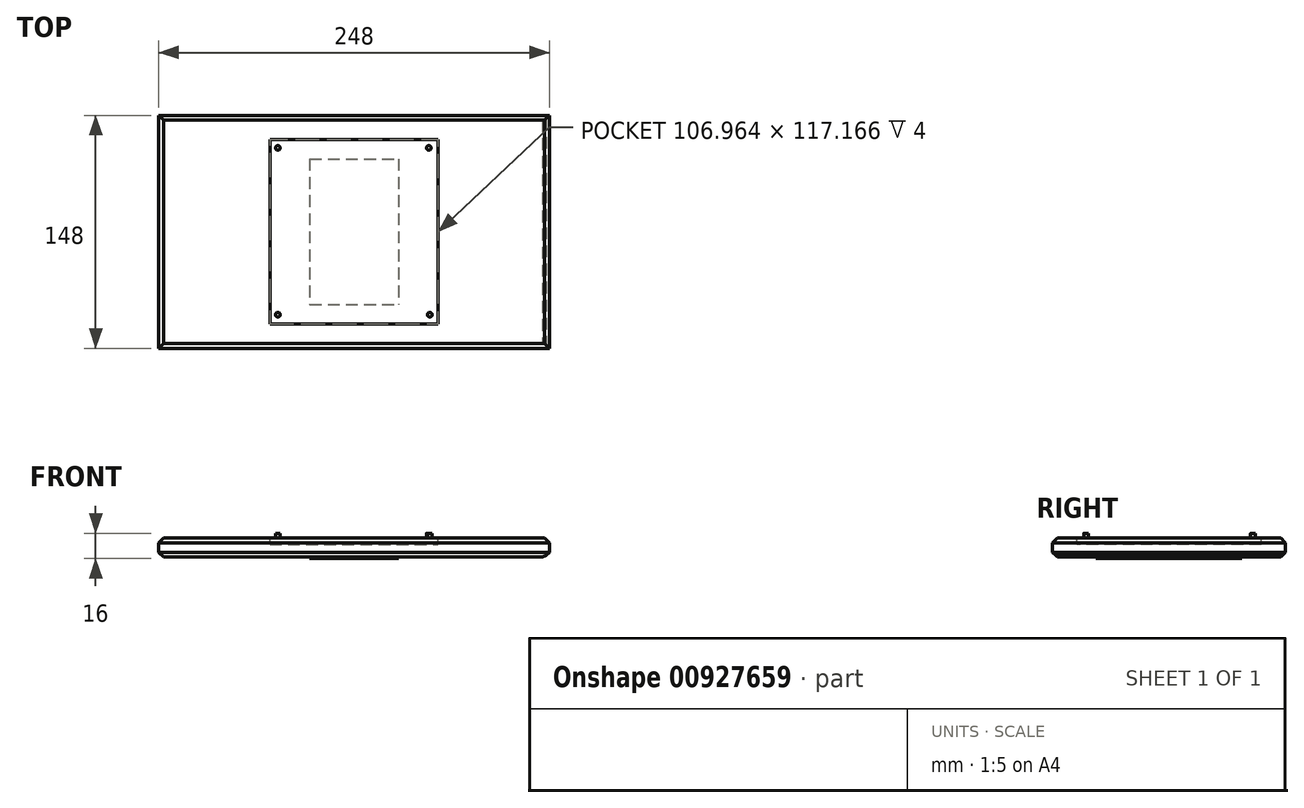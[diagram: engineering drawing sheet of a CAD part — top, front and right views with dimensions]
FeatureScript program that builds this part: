
annotation { "Feature Type Name" : "Feature", "Feature Type Description" : "" }
export const myFeature = defineFeature(function(context is Context, id is Id, definition is map)
    precondition{}
    {
        {
            var Q0;
            Q0=qCreatedBy(makeId("Top.planeOp"),FACE);
            var sketch = newSketch(context, id + "F0", { "sketchPlane" : qUnion([Q0])});
            skLineSegment(sketch, "E0.bottom", {"start": v(-124, -74) * mm, "end": v(124, -74) * mm});
            skLineSegment(sketch, "E0.top", {"start": v(-124, 74) * mm, "end": v(124, 74) * mm});
            skLineSegment(sketch, "E0.left", {"start": v(-124, -74) * mm, "end": v(-124, 74) * mm});
            skLineSegment(sketch, "E0.right", {"start": v(124, -74) * mm, "end": v(124, 74) * mm});
            skPoint(sketch, "E0.middle", {"position": v(0, 0) * mm});
            skSolve(sketch);
        }
        {
            var Q0;
            Q0 = qSketchRegion(id + "F0", true);
            extrude(context, id + "F1", {"entities" : qUnion([Q0]), "depth" : 12 * mm, "offsetDistance" : 25 * mm});
        }
        {
            var Q0;
            Q0=makeQuery(id+"F1.opExtrude","CAP_EDGE",EDGE,{"disambiguationData":[OSD([sQuery(id+"F0.wireOp",EDGE,"E0.top")])],"isStart":false});
            var Q1;
            Q1=makeQuery(id+"F1.opExtrude","CAP_EDGE",EDGE,{"disambiguationData":[OSD([sQuery(id+"F0.wireOp",EDGE,"E0.left")])],"isStart":false});
            var Q2;
            Q2=makeQuery(id+"F1.opExtrude","CAP_EDGE",EDGE,{"disambiguationData":[OSD([sQuery(id+"F0.wireOp",EDGE,"E0.bottom")])],"isStart":false});
            var Q3;
            Q3=makeQuery(id+"F1.opExtrude","CAP_EDGE",EDGE,{"disambiguationData":[OSD([sQuery(id+"F0.wireOp",EDGE,"E0.right")])],"isStart":true});
            chamfer(context, id + "F2", {"entities" : qUnion([Q0, Q1, Q2, Q3]), "width" : 3 * mm, "tangentPropagation" : true});
        }
        {
            var Q0;
            Q0=makeQuery(id+"F1.opExtrude","CAP_EDGE",EDGE,{"disambiguationData":[OSD([sQuery(id+"F0.wireOp",EDGE,"E0.left")])],"isStart":true});
            var Q1;
            Q1=makeQuery(id+"F1.opExtrude","CAP_EDGE",EDGE,{"disambiguationData":[OSD([sQuery(id+"F0.wireOp",EDGE,"E0.top")])],"isStart":true});
            var Q2;
            Q2=makeQuery(id+"F1.opExtrude","CAP_EDGE",EDGE,{"disambiguationData":[OSD([sQuery(id+"F0.wireOp",EDGE,"E0.bottom")])],"isStart":true});
            var Q3;
            {var subQ0=sQuery(id+"F0.wireOp",EDGE,"E0.right");Q3=makeQuery(id+"F2.opChamfer","BLEND_EDGE",EDGE,{"blendedFrom":[makeQuery(id+"F1.opExtrude","CAP_EDGE",EDGE,{"disambiguationData":[OSD([subQ0])],"isStart":true}),makeQuery(id+"F1.opExtrude","CAP_FACE",FACE,{"disambiguationData":[OSD([sQuery(id+"F0.wireOp",EDGE,"E0.bottom"),sQuery(id+"F0.wireOp",EDGE,"E0.top"),sQuery(id+"F0.wireOp",EDGE,"E0.left"),subQ0])],"isStart":true})],"blendedInto":[makeQuery(id+"F1.opExtrude","CAP_FACE",FACE,{"disambiguationData":[OSD([sQuery(id+"F0.wireOp",EDGE,"E0.bottom"),sQuery(id+"F0.wireOp",EDGE,"E0.top"),sQuery(id+"F0.wireOp",EDGE,"E0.left"),subQ0])],"isStart":true})]});}
            chamfer(context, id + "F3", {"entities" : qUnion([Q0, Q1, Q2, Q3]), "width" : 3 * mm, "tangentPropagation" : true});
        }
        {
            var Q0;
            Q0=qCreatedBy(makeId("Top.planeOp"),FACE);
            var sketch = newSketch(context, id + "F4", { "sketchPlane" : qUnion([Q0])});
            skLineSegment(sketch, "E1.bottom", {"start": v(-28.16, 46.29) * mm, "end": v(28.16, 46.29) * mm});
            skLineSegment(sketch, "E1.top", {"start": v(-28.16, -46.29) * mm, "end": v(28.16, -46.29) * mm});
            skLineSegment(sketch, "E1.left", {"start": v(-28.16, 46.29) * mm, "end": v(-28.16, -46.29) * mm});
            skLineSegment(sketch, "E1.right", {"start": v(28.16, 46.29) * mm, "end": v(28.16, -46.29) * mm});
            skPoint(sketch, "E1.middle", {"position": v(0, 0) * mm});
            skSolve(sketch);
        }
        {
            var Q0;
            Q0 = qSketchRegion(id + "F4", true);
            extrude(context, id + "F5", {"entities" : qUnion([Q0]), "oppositeDirection" : true, "depth" : 1 * mm, "offsetDistance" : 25 * mm});
        }
        {
            var Q0;
            Q0=makeQuery(id+"F1.opExtrude","CAP_FACE",FACE,{"disambiguationData":[OSD([sQuery(id+"F0.wireOp",EDGE,"E0.bottom"),sQuery(id+"F0.wireOp",EDGE,"E0.top"),sQuery(id+"F0.wireOp",EDGE,"E0.left"),sQuery(id+"F0.wireOp",EDGE,"E0.right")])],"isStart":false});
            var sketch = newSketch(context, id + "F6", { "sketchPlane" : qUnion([Q0])});
            skLineSegment(sketch, "E2.bottom", {"start": v(-53.48, 58.58) * mm, "end": v(53.48, 58.58) * mm});
            skLineSegment(sketch, "E2.top", {"start": v(-53.48, -58.58) * mm, "end": v(53.48, -58.58) * mm});
            skLineSegment(sketch, "E2.left", {"start": v(-53.48, 58.58) * mm, "end": v(-53.48, -58.58) * mm});
            skLineSegment(sketch, "E2.right", {"start": v(53.48, 58.58) * mm, "end": v(53.48, -58.58) * mm});
            skPoint(sketch, "E2.middle", {"position": v(0, 0) * mm});
            skSolve(sketch);
        }
        {
            var Q0;
            Q0 = qSketchRegion(id + "F6", true);
            extrude(context, id + "F7", {"entities" : qUnion([Q0]), "operationType" : NewBodyOperationType.REMOVE, "oppositeDirection" : true, "depth" : 4 * mm, "offsetDistance" : 25 * mm});
        }
        {
            var Q0;
            Q0=makeQuery(id+"F7.boolean.opBoolean","COPY",FACE,{"derivedFrom":makeQuery(id+"F7.opExtrude","CAP_FACE",FACE,{"disambiguationData":[OSD([sQuery(id+"F6.wireOp",EDGE,"E2.bottom"),sQuery(id+"F6.wireOp",EDGE,"E2.top"),sQuery(id+"F6.wireOp",EDGE,"E2.left"),sQuery(id+"F6.wireOp",EDGE,"E2.right")])],"isStart":false})});
            var sketch = newSketch(context, id + "F8", { "sketchPlane" : qUnion([Q0])});
            skSolve(sketch);
        }
        {
            var Q0;
            Q0=makeQuery(id+"F8.imprint","IMPRINT",FACE,{"disambiguationData":[TD([[makeQuery(id+"F8.imprint","IMPRINT",EDGE,{"derivedFrom":makeQuery(id+"F7.boolean.opBoolean","COPY",EDGE,{"derivedFrom":makeQuery(id+"F7.opExtrude","CAP_EDGE",EDGE,{"disambiguationData":[OSD([sQuery(id+"F6.wireOp",EDGE,"E2.bottom")])],"isStart":false})})}),-1.0]])]});
            extrude(context, id + "F9", {"entities" : qUnion([Q0]), "depth" : 4 * mm, "offsetDistance" : 25 * mm});
        }
        {
            var Q0;
            Q0=makeQuery(id+"F9.opExtrude","CAP_FACE",FACE,{"disambiguationData":[OSD([sQuery(id+"F6.wireOp",EDGE,"E2.bottom"),sQuery(id+"F6.wireOp",EDGE,"E2.top"),sQuery(id+"F6.wireOp",EDGE,"E2.left"),sQuery(id+"F6.wireOp",EDGE,"E2.right")])],"isStart":false});
            var sketch = newSketch(context, id + "F10", { "sketchPlane" : qUnion([Q0])});
            skCircle(sketch, "E3", {"center": v(-48.41, 53.3) * mm, "radius": 1.5 * mm});
            skSolve(sketch);
        }
        {
            var Q0;
            Q0 = qSketchRegion(id + "F10", true);
            extrude(context, id + "F11", {"entities" : qUnion([Q0]), "depth" : 3 * mm, "offsetDistance" : 25 * mm});
        }
        {
            var Q0;
            Q0=makeQuery(id+"F11.opExtrude","SWEPT_BODY",BODY,{"disambiguationData":[OSD([sQuery(id+"F10.wireOp",EDGE,"E3")])]});
            transform(context, id + "F12", {"entities" : qUnion([Q0]), "transformType" : TransformType.TRANSLATION_3D, "dx" : 0 * mm, "dy" : 0 * mm, "dz" : 0 * mm, "makeCopy" : true});
        }
        {
            var Q0;
            Q0=makeQuery(id+"F12.opPattern","COPY",BODY,{"derivedFrom":makeQuery(id+"F11.opExtrude","SWEPT_BODY",BODY,{"disambiguationData":[OSD([sQuery(id+"F10.wireOp",EDGE,"E3")])]}),"instanceName":"1"});
            deleteBodies(context, id + "F13", {"entities" : qUnion([Q0])});
        }
        {
            var Q0;
            Q0=makeQuery(id+"F11.opExtrude","SWEPT_BODY",BODY,{"disambiguationData":[OSD([sQuery(id+"F10.wireOp",EDGE,"E3")])]});
            transform(context, id + "F14", {"entities" : qUnion([Q0]), "transformType" : TransformType.TRANSLATION_3D, "dx" : 95.9 * mm, "dy" : 0 * mm, "dz" : 0 * mm, "makeCopy" : true});
        }
        {
            var Q0;
            Q0=makeQuery(id+"F11.opExtrude","SWEPT_BODY",BODY,{"disambiguationData":[OSD([sQuery(id+"F10.wireOp",EDGE,"E3")])]});
            transform(context, id + "F15", {"entities" : qUnion([Q0]), "transformType" : TransformType.TRANSLATION_3D, "dx" : 0 * mm, "dy" : -105.9 * mm, "dz" : 0 * mm, "makeCopy" : true});
        }
        {
            var Q0;
            Q0=makeQuery(id+"F15.opPattern","COPY",BODY,{"derivedFrom":makeQuery(id+"F11.opExtrude","SWEPT_BODY",BODY,{"disambiguationData":[OSD([sQuery(id+"F10.wireOp",EDGE,"E3")])]}),"instanceName":"1"});
            transform(context, id + "F16", {"entities" : qUnion([Q0]), "transformType" : TransformType.TRANSLATION_3D, "dx" : 96.5 * mm, "dy" : 0 * mm, "dz" : 0 * mm, "makeCopy" : true});
        }
        {
            var Q0;
            Q0=makeQuery(id+"F1.opExtrude","CAP_EDGE",EDGE,{"disambiguationData":[OSD([sQuery(id+"F0.wireOp",EDGE,"E0.right")])],"isStart":false});
            chamfer(context, id + "F17", {"entities" : qUnion([Q0]), "width" : 3 * mm, "tangentPropagation" : true});
        }
    });
